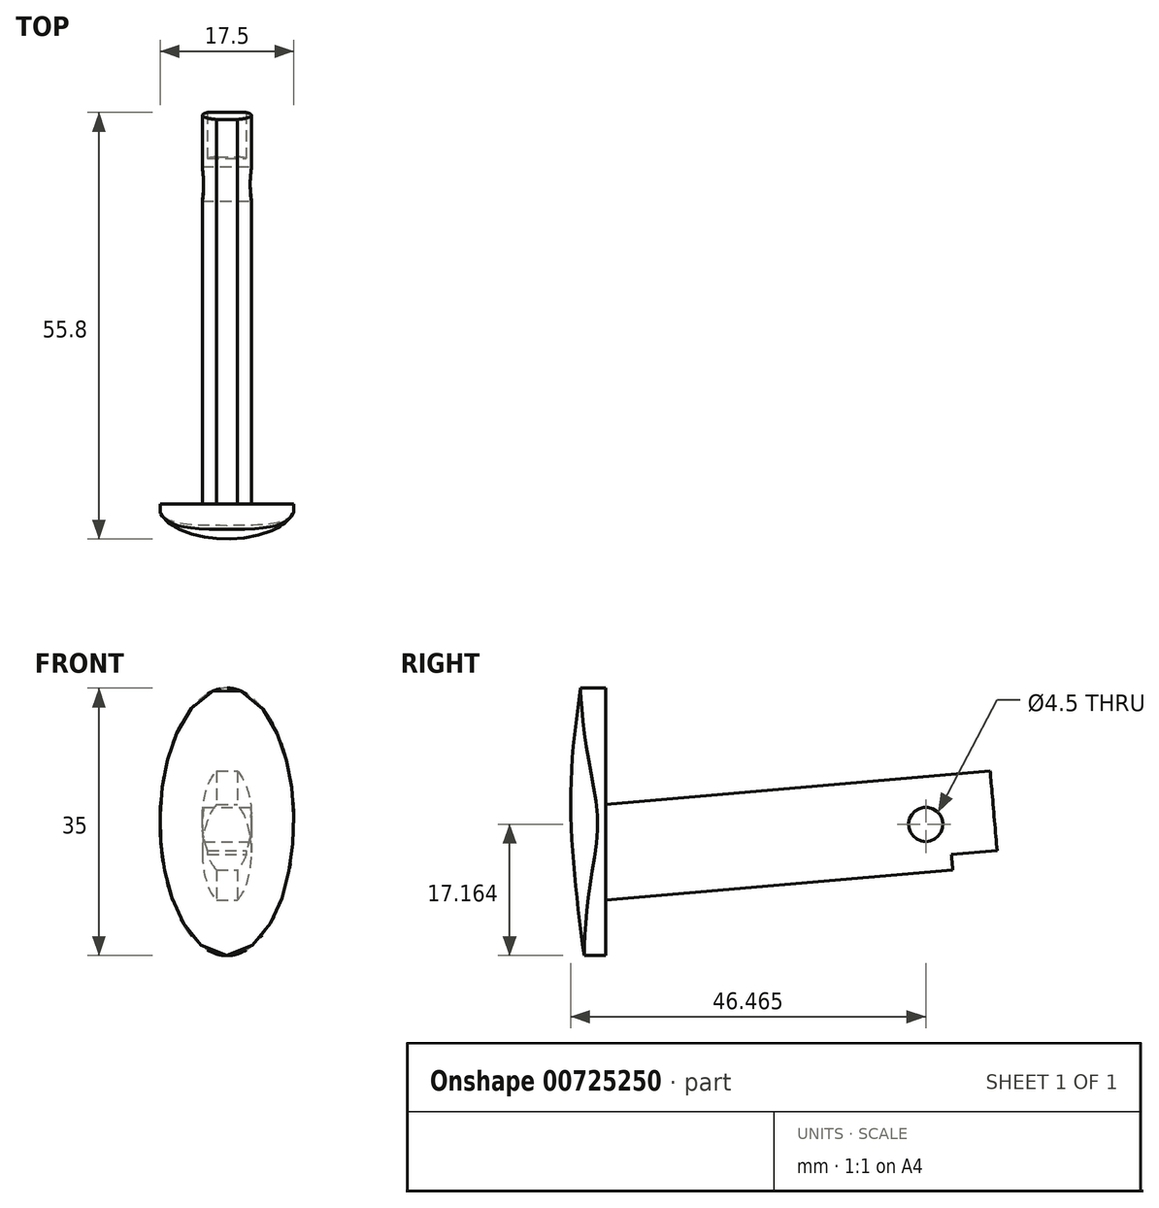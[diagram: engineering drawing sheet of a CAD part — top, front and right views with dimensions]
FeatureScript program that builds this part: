
annotation { "Feature Type Name" : "Feature", "Feature Type Description" : "" }
export const myFeature = defineFeature(function(context is Context, id is Id, definition is map)
    precondition{}
    {
        {
            var Q0;
            Q0=qCreatedBy(makeId("Front.planeOp"),FACE);
            var sketch = newSketch(context, id + "F0", { "sketchPlane" : qUnion([Q0])});
            skEllipse(sketch, "E0", {"center": v(0, 0) * mm, "majorRadius": 17.5 * mm, "minorRadius": 8.75 * mm, "majorAxis": v(0, -1)});
            skSolve(sketch);
        }
        {
            var Q0;
            Q0=makeQuery(id+"F0.imprint","IMPRINT",FACE,{"disambiguationData":[TD([[makeQuery(id+"F0.imprint","IMPRINT",EDGE,{"derivedFrom":sQuery(id+"F0.wireOp",EDGE,"E0")}),1.0]])]});
            extrude(context, id + "F1", {"entities" : qUnion([Q0]), "depth" : 5 * mm, "offsetDistance" : 25 * mm});
        }
        {
            var Q0;
            Q0=qCreatedBy(makeId("Right.planeOp"),FACE);
            var sketch = newSketch(context, id + "F2", { "sketchPlane" : qUnion([Q0])});
            skPoint(sketch, "E1", {"position": v(-5, -17.5) * mm});
            skLineSegment(sketch, "E2.0", {"start": v(-5, 17.5) * mm, "end": v(-5, -17.5) * mm});
            skFitSpline(sketch, "E3", {"points": [v(-3.32, 17.5) * mm, v(-5, 3.08) * mm, v(-2.83, -17.5) * mm], "startDerivative": vector(-7.4, -20) * mm, "endDerivative": vector(6.97, -29.38) * mm});
            skLineSegment(sketch, "E4", {"start": v(-3.32, 17.5) * mm, "end": v(-5, 17.5) * mm});
            skLineSegment(sketch, "E5", {"start": v(-5, -17.5) * mm, "end": v(-2.83, -17.5) * mm});
            skSolve(sketch);
        }
        {
            var Q0;
            Q0 = qSketchRegion(id + "F2", true);
            extrude(context, id + "F3", {"entities" : qUnion([Q0]), "operationType" : NewBodyOperationType.REMOVE, "endBound" : BoundingType.THROUGH_ALL, "oppositeDirection" : true, "depth" : 25 * mm, "offsetDistance" : 25 * mm, "hasSecondDirection" : true, "secondDirectionBound" : SecondDirectionBoundingType.THROUGH_ALL, "secondDirectionOppositeDirection" : false, "secondDirectionDepth" : 25 * mm});
        }
        {
            var Q0;
            Q0=qCreatedBy(makeId("Top.planeOp"),FACE);
            cPlane(context, id + "F4", {"entities" : qUnion([Q0]), "cplaneType" : CPlaneType.OFFSET, "offset" : 6.2 * mm, "width" : 150 * mm, "height" : 150 * mm});
        }
        {
            var Q0;
            {var subQ0=sQuery(id+"F2.wireOp",EDGE,"E3");Q0=makeQuery(id+"F3.boolean.opBoolean","INTERSECT",EDGE,{"derivedFrom":[makeQuery(id+"F1.opExtrude","SWEPT_FACE",FACE,{"disambiguationData":[OSD([sQuery(id+"F0.wireOp",EDGE,"E0")])]}),makeQuery(id+"F3.opExtrude","SWEPT_FACE",FACE,{"disambiguationData":[OSD([subQ0]),TDD([makeQuery(id+"F2.imprint","IMPRINT",EDGE,{"disambiguationData":[TD([[makeQuery(id+"F2.imprint","INTERSECT",VERTEX,{"derivedFrom":[subQ0,sQuery(id+"F2.wireOp",EDGE,"E4")]}),-1.0]])],"derivedFrom":subQ0})])]})]});}
            cPoint(context, id + "F5", {"entities" : qUnion([Q0]), "parameter" : 0.5});
        }
        {
            var Q0;
            Q0 = qCreatedBy(id + "F5" ,VERTEX);
            var Q1;
            Q1=qCreatedBy(makeId("Top.planeOp"),FACE);
            cPlane(context, id + "F6", {"entities" : qUnion([Q0, Q1]), "cplaneType" : CPlaneType.PLANE_POINT, "offset" : 25 * mm, "width" : 150 * mm, "height" : 150 * mm});
        }
        {
            var Q0;
            {var subQ0=sQuery(id+"F2.wireOp",EDGE,"E3");Q0=makeQuery(id+"F3.boolean.opBoolean","INTERSECT",EDGE,{"derivedFrom":[makeQuery(id+"F1.opExtrude","SWEPT_FACE",FACE,{"disambiguationData":[OSD([sQuery(id+"F0.wireOp",EDGE,"E0")])]}),makeQuery(id+"F3.opExtrude","SWEPT_FACE",FACE,{"disambiguationData":[OSD([subQ0]),TDD([makeQuery(id+"F2.imprint","IMPRINT",EDGE,{"disambiguationData":[TD([[makeQuery(id+"F2.imprint","INTERSECT",VERTEX,{"derivedFrom":[subQ0,sQuery(id+"F2.wireOp",EDGE,"E5")]}),1.0]])],"derivedFrom":subQ0})])]})]});}
            cPoint(context, id + "F7", {"entities" : qUnion([Q0]), "parameter" : 0.5});
        }
        {
            var Q0;
            Q0 = qCreatedBy(id + "F7" ,VERTEX);
            var Q1;
            Q1=qCreatedBy(makeId("Top.planeOp"),FACE);
            var Q2;
            Q2 = qBodyType(qCreatedBy(id + "F11" ,EDGE), BodyType.WIRE);
            cPlane(context, id + "F8", {"entities" : qUnion([Q0, Q1, Q2]), "cplaneType" : CPlaneType.PLANE_POINT, "offset" : 25 * mm, "width" : 150 * mm, "height" : 150 * mm});
        }
        {
            var Q0;
            Q0=qCreatedBy(id+"F4.planeOp",FACE);
            var sketch = newSketch(context, id + "F9", { "sketchPlane" : qUnion([Q0])});
            skEllipse(sketch, "E6", {"center": v(0, 0) * mm, "majorRadius": 4.5 * mm, "minorRadius": 9 * mm, "majorAxis": v(0, -1)});
            skSolve(sketch);
        }
        {
            var Q0;
            Q0=qCreatedBy(id+"F6.planeOp",FACE);
            var sketch = newSketch(context, id + "F10", { "sketchPlane" : qUnion([Q0])});
            skEllipse(sketch, "E7", {"center": v(0, 0) * mm, "majorRadius": 3.32 * mm, "minorRadius": 9 * mm, "majorAxis": v(0, -1)});
            skSolve(sketch);
        }
        {
            var Q0;
            Q0=qCreatedBy(id+"F8.planeOp",FACE);
            var sketch = newSketch(context, id + "F11", { "sketchPlane" : qUnion([Q0])});
            skEllipse(sketch, "E8", {"center": v(0, 0) * mm, "majorRadius": 2.83 * mm, "minorRadius": 9 * mm, "majorAxis": v(0, -1)});
            skSolve(sketch);
        }
        {
            var Q1;
            Q1=makeQuery(id+"F10.imprint","IMPRINT",FACE,{"disambiguationData":[TD([[makeQuery(id+"F10.imprint","IMPRINT",EDGE,{"derivedFrom":sQuery(id+"F10.wireOp",EDGE,"E7")}),1.0]])]});
            var Q2;
            Q2=makeQuery(id+"F9.imprint","IMPRINT",FACE,{"disambiguationData":[TD([[makeQuery(id+"F9.imprint","IMPRINT",EDGE,{"derivedFrom":sQuery(id+"F9.wireOp",EDGE,"E6")}),1.0]])]});
            var Q3;
            Q3=makeQuery(id+"F11.imprint","IMPRINT",FACE,{"disambiguationData":[TD([[makeQuery(id+"F11.imprint","IMPRINT",EDGE,{"derivedFrom":sQuery(id+"F11.wireOp",EDGE,"E8")}),1.0]])]});
            loft(context, id + "F12", {"operationType" : NewBodyOperationType.INTERSECT, "sheetProfilesArray" : [{ "sheetProfileEntities" : qUnion([Q1]) }, { "sheetProfileEntities" : qUnion([Q2]) }, { "sheetProfileEntities" : qUnion([Q3]) }]});
        }
        {
            var Q0;
            Q0=makeQuery(id+"F1.opExtrude","CAP_FACE",FACE,{"disambiguationData":[OSD([sQuery(id+"F0.wireOp",EDGE,"E0")])],"isStart":true});
            var sketch = newSketch(context, id + "F13", { "sketchPlane" : qUnion([Q0])});
            skLineSegment(sketch, "E9", {"start": v(8.68, 2.25) * mm, "end": v(-8.68, 2.25) * mm});
            skLineSegment(sketch, "E10", {"start": v(0, 0) * mm, "end": v(0, 17.5) * mm, "construction": true});
            skLineSegment(sketch, "E11", {"start": v(-7.1, -10.25) * mm, "end": v(7.1, -10.25) * mm});
            skLineSegment(sketch, "E12", {"start": v(0, 0) * mm, "end": v(0, -17.5) * mm, "construction": true});
            skSolve(sketch);
        }
        {
            var Q0;
            Q0=sQuery(id+"F13.wireOp",EDGE,"E9");
            cPlane(context, id + "F14", {"entities" : qUnion([Q0]), "cplaneType" : CPlaneType.LINE_ANGLE, "offset" : 25 * mm, "angle" : 5 * degree, "width" : 150 * mm, "height" : 150 * mm});
        }
        {
            var Q0;
            Q0=qCreatedBy(id+"F14.planeOp",FACE);
            var sketch = newSketch(context, id + "F15", { "sketchPlane" : qUnion([Q0])});
            skLineSegment(sketch, "E13", {"start": v(0, -10.21) * mm, "end": v(0, 2.24) * mm, "construction": true});
            skEllipse(sketch, "E14", {"center": v(0, -3.98) * mm, "majorRadius": 3.22 * mm, "minorRadius": 6.85 * mm, "majorAxis": v(1, 0)});
            skLineSegment(sketch, "E15", {"start": v(1.35, 2.24) * mm, "end": v(1.35, 2.24) * mm});
            skLineSegment(sketch, "E16", {"start": v(1.35, -10.21) * mm, "end": v(1.35, -10.21) * mm});
            skLineSegment(sketch, "E17", {"start": v(1.35, 2.24) * mm, "end": v(-1.35, 2.24) * mm});
            skLineSegment(sketch, "E18", {"start": v(-1.35, -10.21) * mm, "end": v(1.35, -10.21) * mm});
            skSolve(sketch);
        }
        {
            var Q0;
            {var subQ0=sQuery(id+"F15.wireOp",EDGE,"E17");Q0=makeQuery(id+"F15.imprint","IMPRINT",FACE,{"disambiguationData":[TD([[makeQuery(id+"F15.imprint","IMPRINT",EDGE,{"derivedFrom":subQ0}),1.0]])]});}
            extrude(context, id + "F16", {"entities" : qUnion([Q0]), "operationType" : NewBodyOperationType.ADD, "depth" : 50.5 * mm, "offsetDistance" : 25 * mm, "hasSecondDirection" : true, "secondDirectionBound" : SecondDirectionBoundingType.UP_TO_NEXT, "secondDirectionOppositeDirection" : true, "secondDirectionDepth" : 25 * mm});
        }
        {
            var Q0;
            Q0=qCreatedBy(makeId("Right.planeOp"),FACE);
            var sketch = newSketch(context, id + "F17", { "sketchPlane" : qUnion([Q0])});
            skLineSegment(sketch, "E19", {"start": v(51.22, -3.76) * mm, "end": v(45.24, -4.28) * mm});
            skLineSegment(sketch, "E20", {"start": v(45.24, -4.28) * mm, "end": v(45.42, -6.28) * mm});
            skLineSegment(sketch, "E21", {"start": v(51.22, -3.76) * mm, "end": v(51.4, -5.75) * mm});
            skLineSegment(sketch, "E22", {"start": v(51.4, -5.75) * mm, "end": v(45.42, -6.28) * mm});
            skLineSegment(sketch, "E23", {"start": v(49.4, 0.32) * mm, "end": v(29.27, -1.44) * mm, "construction": true});
            skCircle(sketch, "E24", {"center": v(41.88, -0.34) * mm, "radius": 2.25 * mm});
            skSolve(sketch);
        }
        {
            var Q0;
            Q0 = qSketchRegion(id + "F17", true);
            extrude(context, id + "F18", {"entities" : qUnion([Q0]), "operationType" : NewBodyOperationType.REMOVE, "endBound" : BoundingType.THROUGH_ALL, "oppositeDirection" : true, "depth" : 25 * mm, "offsetDistance" : 25 * mm, "hasSecondDirection" : true, "secondDirectionBound" : SecondDirectionBoundingType.THROUGH_ALL, "secondDirectionOppositeDirection" : false, "secondDirectionDepth" : 25 * mm});
        }
    });
